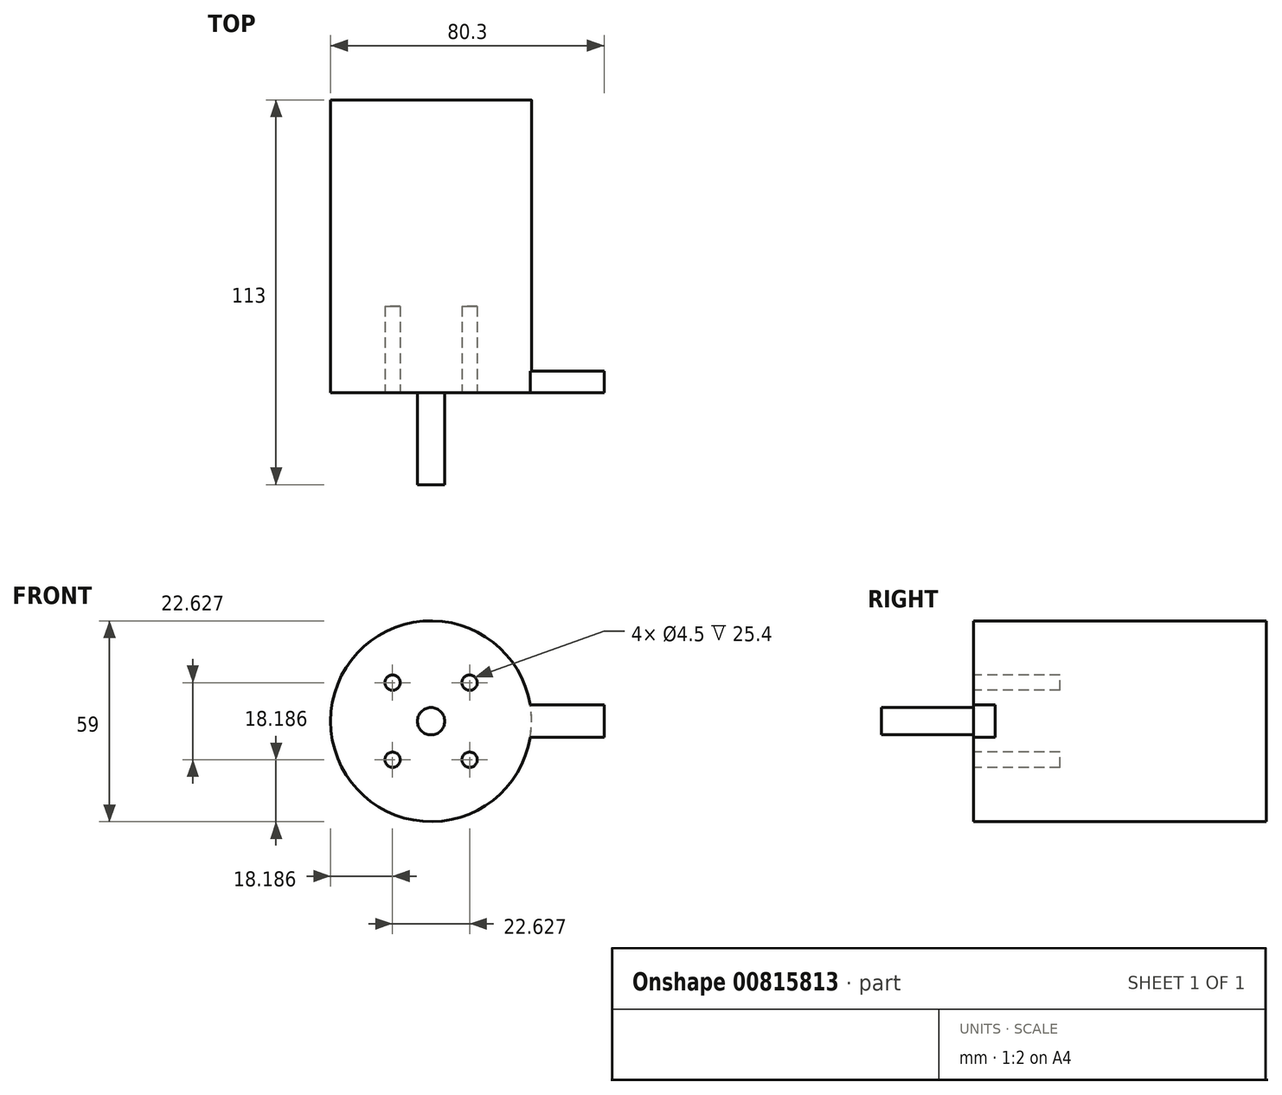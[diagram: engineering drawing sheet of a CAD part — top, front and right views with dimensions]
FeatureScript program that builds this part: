
annotation { "Feature Type Name" : "Feature", "Feature Type Description" : "" }
export const myFeature = defineFeature(function(context is Context, id is Id, definition is map)
    precondition{}
    {
        {
            var Q0;
            Q0=qCreatedBy(makeId("Front.planeOp"),FACE);
            var sketch = newSketch(context, id + "F0", { "sketchPlane" : qUnion([Q0])});
            skCircle(sketch, "E0", {"center": v(0, 0) * mm, "radius": 29.5 * mm});
            skSolve(sketch);
        }
        {
            var Q0;
            Q0 = qSketchRegion(id + "F0", true);
            extrude(context, id + "F1", {"entities" : qUnion([Q0]), "depth" : 86 * mm, "offsetDistance" : 25.4 * mm});
        }
        {
            var Q0;
            Q0=makeQuery(id+"F1.opExtrude","CAP_FACE",FACE,{"disambiguationData":[OSD([sQuery(id+"F0.wireOp",EDGE,"E0")])],"isStart":false});
            var sketch = newSketch(context, id + "F2", { "sketchPlane" : qUnion([Q0])});
            skCircle(sketch, "E1", {"center": v(0, 0) * mm, "radius": 4 * mm});
            skSolve(sketch);
        }
        {
            var Q0;
            Q0 = qSketchRegion(id + "F2", true);
            extrude(context, id + "F3", {"entities" : qUnion([Q0]), "operationType" : NewBodyOperationType.ADD, "depth" : 113 * mm - 86 * mm, "offsetDistance" : 25.4 * mm});
        }
        {
            var Q0;
            Q0=makeQuery(id+"F1.opExtrude","CAP_FACE",FACE,{"disambiguationData":[OSD([sQuery(id+"F0.wireOp",EDGE,"E0")])],"isStart":false});
            var sketch = newSketch(context, id + "F4", { "sketchPlane" : qUnion([Q0])});
            skCircle(sketch, "E2", {"center": v(11.31, 11.31) * mm, "radius": 2.25 * mm});
            skCircle(sketch, "E3.1.0", {"center": v(-11.31, 11.31) * mm, "radius": 2.25 * mm});
            skCircle(sketch, "E3.2.0", {"center": v(-11.31, -11.31) * mm, "radius": 2.25 * mm});
            skCircle(sketch, "E3.3.0", {"center": v(11.31, -11.31) * mm, "radius": 2.25 * mm});
            skPoint(sketch, "E3.center", {"position": v(0, 0) * mm});
            skLineSegment(sketch, "E4", {"start": v(0, 0) * mm, "end": v(0, 15.22) * mm});
            skLineSegment(sketch, "E5", {"start": v(0, 0) * mm, "end": v(11.31, 11.31) * mm});
            skSolve(sketch);
        }
        {
            var Q0;
            Q0=qCreatedBy(makeId("Right.planeOp"),FACE);
            var sketch = newSketch(context, id + "F5", { "sketchPlane" : qUnion([Q0])});
            skLineSegment(sketch, "E6.bottom", {"start": v(-86, -4.76) * mm, "end": v(-79.65, -4.76) * mm});
            skLineSegment(sketch, "E6.top", {"start": v(-86, 4.76) * mm, "end": v(-79.65, 4.76) * mm});
            skLineSegment(sketch, "E6.left", {"start": v(-86, -4.76) * mm, "end": v(-86, 4.76) * mm});
            skLineSegment(sketch, "E6.right", {"start": v(-79.65, -4.76) * mm, "end": v(-79.65, 4.76) * mm});
            skSolve(sketch);
        }
        {
            var Q0;
            Q0 = qSketchRegion(id + "F5", true);
            extrude(context, id + "F6", {"entities" : qUnion([Q0]), "operationType" : NewBodyOperationType.ADD, "depth" : 50.8 * mm, "offsetDistance" : 25.4 * mm});
        }
        {
            var Q0;
            Q0 = qSketchRegion(id + "F4", true);
            extrude(context, id + "F7", {"entities" : qUnion([Q0]), "operationType" : NewBodyOperationType.REMOVE, "oppositeDirection" : true, "depth" : 25.4 * mm, "offsetDistance" : 25.4 * mm});
        }
    });
